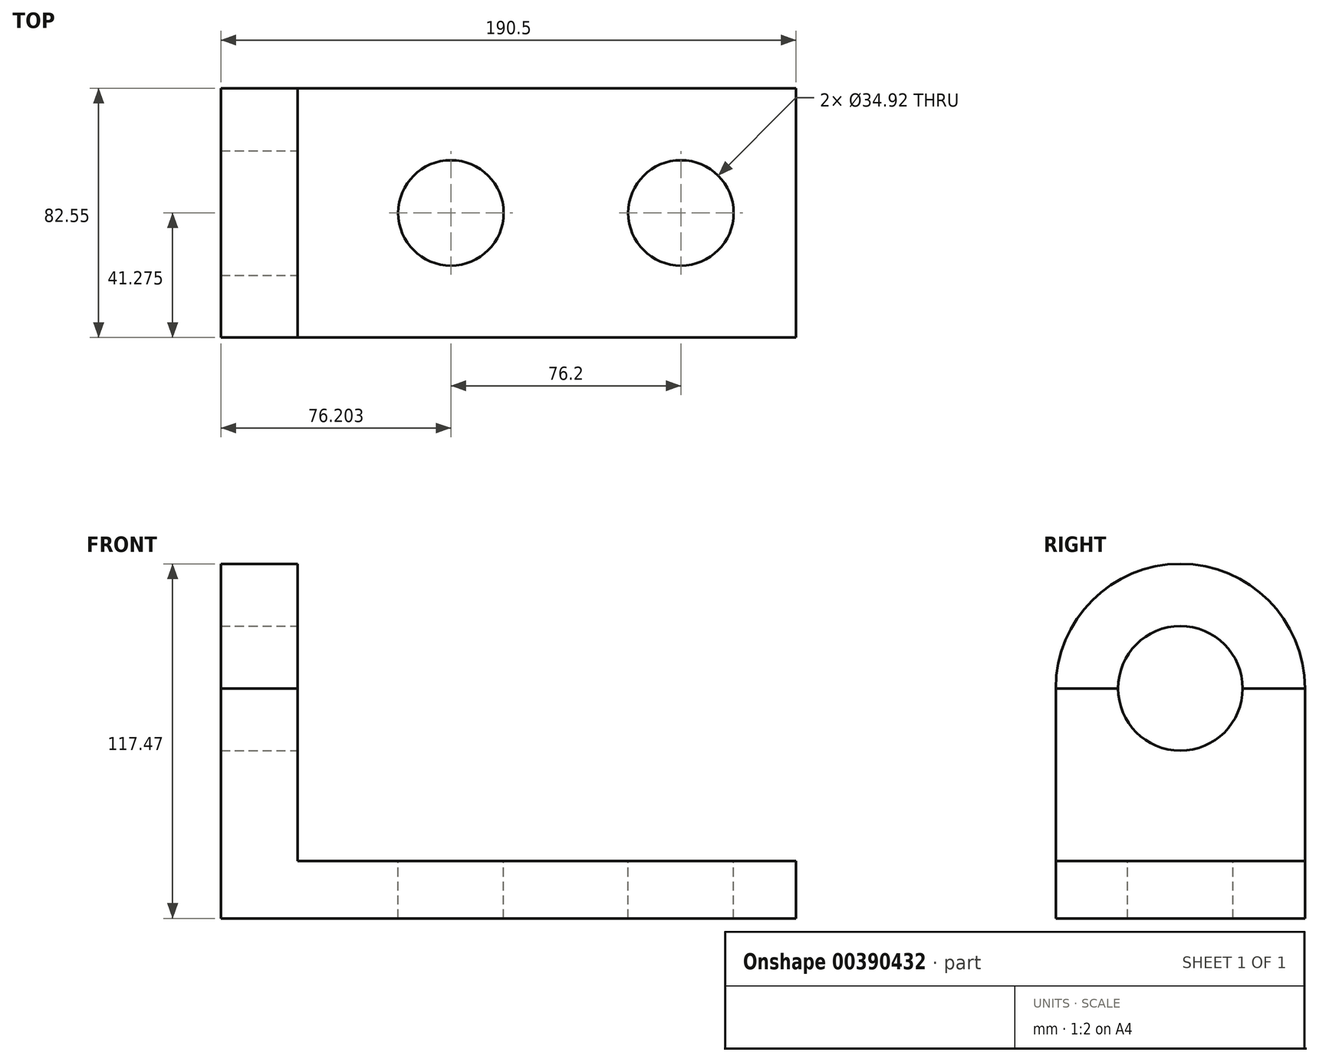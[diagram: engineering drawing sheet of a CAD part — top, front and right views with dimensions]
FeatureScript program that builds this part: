
annotation { "Feature Type Name" : "Feature", "Feature Type Description" : "" }
export const myFeature = defineFeature(function(context is Context, id is Id, definition is map)
    precondition{}
    {
        {
            var Q0;
            Q0=qCreatedBy(makeId("Top.planeOp"),FACE);
            var sketch = newSketch(context, id + "F0", { "sketchPlane" : qUnion([Q0])});
            skLineSegment(sketch, "E0", {"start": v(-43.38, 45.06) * mm, "end": v(-43.38, -37.5) * mm});
            skLineSegment(sketch, "E1", {"start": v(-43.38, -37.5) * mm, "end": v(147.12, -37.5) * mm});
            skLineSegment(sketch, "E2", {"start": v(147.12, -37.5) * mm, "end": v(147.12, 45.06) * mm});
            skLineSegment(sketch, "E3", {"start": v(147.12, 45.06) * mm, "end": v(-43.38, 45.06) * mm});
            skSolve(sketch);
        }
        {
            var Q0;
            Q0=makeQuery(id+"F0.imprint","IMPRINT",FACE,{"disambiguationData":[TD([[makeQuery(id+"F0.imprint","IMPRINT",EDGE,{"derivedFrom":sQuery(id+"F0.wireOp",EDGE,"E0")}),1.0]])]});
            extrude(context, id + "F1", {"entities" : qUnion([Q0]), "depth" : 19.05 * mm});
        }
        {
            var Q0;
            Q0=makeQuery(id+"F1.opExtrude","CAP_FACE",FACE,{"disambiguationData":[OSD([sQuery(id+"F0.wireOp",EDGE,"E0"),sQuery(id+"F0.wireOp",EDGE,"E1"),sQuery(id+"F0.wireOp",EDGE,"E2"),sQuery(id+"F0.wireOp",EDGE,"E3")])],"isStart":false});
            var sketch = newSketch(context, id + "F2", { "sketchPlane" : qUnion([Q0])});
            skLineSegment(sketch, "E4", {"start": v(-43.38, 45.06) * mm, "end": v(-17.98, 45.06) * mm});
            skLineSegment(sketch, "E5", {"start": v(-17.98, 45.06) * mm, "end": v(-17.98, -37.5) * mm});
            skLineSegment(sketch, "E6", {"start": v(-17.98, -37.5) * mm, "end": v(-43.38, -37.5) * mm});
            skLineSegment(sketch, "E7", {"start": v(-43.38, -37.5) * mm, "end": v(-43.38, 45.06) * mm});
            skSolve(sketch);
        }
        {
            var Q0;
            Q0=makeQuery(id+"F2.imprint","IMPRINT",FACE,{"disambiguationData":[TD([[makeQuery(id+"F2.imprint","IMPRINT",EDGE,{"derivedFrom":sQuery(id+"F2.wireOp",EDGE,"E4")}),1.0]])]});
            extrude(context, id + "F3", {"entities" : qUnion([Q0]), "operationType" : NewBodyOperationType.ADD, "depth" : 57.15 * mm});
        }
        {
            var Q0;
            Q0=makeQuery(id+"F3.opExtrude","SWEPT_FACE",FACE,{"disambiguationData":[OSD([sQuery(id+"F2.wireOp",EDGE,"E5")])]});
            var sketch = newSketch(context, id + "F4", { "sketchPlane" : qUnion([Q0])});
            skCircle(sketch, "E8", {"center": v(3.78, 76.2) * mm, "radius": 41.28 * mm});
            skSolve(sketch);
        }
        {
            var Q0;
            {var subQ1=sQuery(id+"F2.wireOp",EDGE,"E5");var subQ2=makeQuery(id+"F3.opExtrude","CAP_EDGE",EDGE,{"disambiguationData":[OSD([subQ1])],"isStart":false});Q0=makeQuery(id+"F4.imprint","IMPRINT",FACE,{"disambiguationData":[TD([[makeQuery(id+"F4.imprint","IMPRINT",EDGE,{"derivedFrom":subQ2}),-1.0]])]});}
            extrude(context, id + "F5", {"entities" : qUnion([Q0]), "oppositeDirection" : true, "depth" : 25.4 * mm});
        }
        {
            var Q0;
            Q0=makeQuery(id+"F5.opExtrude","CAP_FACE",FACE,{"disambiguationData":[OSD([sQuery(id+"F2.wireOp",EDGE,"E5"),sQuery(id+"F4.wireOp",EDGE,"E8")])],"isStart":true});
            var sketch = newSketch(context, id + "F6", { "sketchPlane" : qUnion([Q0])});
            skCircle(sketch, "E9", {"center": v(3.78, 76.2) * mm, "radius": 20.64 * mm});
            skSolve(sketch);
        }
        {
            var Q0;
            {var subQ0=sQuery(id+"F6.wireOp",EDGE,"E9");var subQ1=makeQuery(id+"F5.opExtrude","CAP_EDGE",EDGE,{"disambiguationData":[OSD([sQuery(id+"F2.wireOp",EDGE,"E5")])],"isStart":true});var subQ2=makeQuery(id+"F6.imprint","INTERSECT",VERTEX,{"disambiguationData":[OD(0.0)],"derivedFrom":[subQ1,subQ0]});Q0=makeQuery(id+"F6.imprint","IMPRINT",FACE,{"disambiguationData":[TD([[makeQuery(id+"F6.imprint","IMPRINT",EDGE,{"disambiguationData":[TD([[subQ2,-1.0]])],"derivedFrom":subQ0}),1.0]])]});}
            extrude(context, id + "F7", {"entities" : qUnion([Q0]), "operationType" : NewBodyOperationType.REMOVE, "oppositeDirection" : true, "depth" : 25.4 * mm});
        }
        {
            var Q0;
            Q0=makeQuery(id+"F3.opExtrude","SWEPT_FACE",FACE,{"disambiguationData":[OSD([sQuery(id+"F2.wireOp",EDGE,"E5")])]});
            var sketch = newSketch(context, id + "F8", { "sketchPlane" : qUnion([Q0])});
            skCircle(sketch, "E10", {"center": v(3.78, 76.2) * mm, "radius": 20.64 * mm});
            skSolve(sketch);
        }
        {
            var Q0;
            {var subQ0=sQuery(id+"F8.wireOp",EDGE,"E10");var subQ1=makeQuery(id+"F3.opExtrude","CAP_EDGE",EDGE,{"disambiguationData":[OSD([sQuery(id+"F2.wireOp",EDGE,"E5")])],"isStart":false});var subQ2=makeQuery(id+"F8.imprint","INTERSECT",VERTEX,{"disambiguationData":[OD(0.0)],"derivedFrom":[subQ1,subQ0]});Q0=makeQuery(id+"F8.imprint","IMPRINT",FACE,{"disambiguationData":[TD([[makeQuery(id+"F8.imprint","IMPRINT",EDGE,{"disambiguationData":[TD([[subQ2,1.0]])],"derivedFrom":subQ0}),1.0]])]});}
            extrude(context, id + "F9", {"entities" : qUnion([Q0]), "operationType" : NewBodyOperationType.REMOVE, "oppositeDirection" : true, "depth" : 25.4 * mm});
        }
        {
            var Q0;
            Q0=makeQuery(id+"F1.opExtrude","CAP_FACE",FACE,{"disambiguationData":[OSD([sQuery(id+"F0.wireOp",EDGE,"E0"),sQuery(id+"F0.wireOp",EDGE,"E1"),sQuery(id+"F0.wireOp",EDGE,"E2"),sQuery(id+"F0.wireOp",EDGE,"E3")])],"isStart":false});
            var sketch = newSketch(context, id + "F10", { "sketchPlane" : qUnion([Q0])});
            skCircle(sketch, "E11", {"center": v(109.02, 3.78) * mm, "radius": 17.46 * mm});
            skSolve(sketch);
        }
        {
            var Q0;
            Q0=makeQuery(id+"F10.imprint","IMPRINT",FACE,{"disambiguationData":[TD([[makeQuery(id+"F10.imprint","IMPRINT",EDGE,{"derivedFrom":sQuery(id+"F10.wireOp",EDGE,"E11")}),1.0]])]});
            extrude(context, id + "F11", {"entities" : qUnion([Q0]), "operationType" : NewBodyOperationType.REMOVE, "oppositeDirection" : true, "depth" : 25.4 * mm});
        }
        {
            var Q0;
            Q0=makeQuery(id+"F1.opExtrude","CAP_FACE",FACE,{"disambiguationData":[OSD([sQuery(id+"F0.wireOp",EDGE,"E0"),sQuery(id+"F0.wireOp",EDGE,"E1"),sQuery(id+"F0.wireOp",EDGE,"E2"),sQuery(id+"F0.wireOp",EDGE,"E3")])],"isStart":false});
            var sketch = newSketch(context, id + "F12", { "sketchPlane" : qUnion([Q0])});
            skCircle(sketch, "E12", {"center": v(32.82, 3.78) * mm, "radius": 17.46 * mm});
            skSolve(sketch);
        }
        {
            var Q0;
            Q0=makeQuery(id+"F12.imprint","IMPRINT",FACE,{"disambiguationData":[TD([[makeQuery(id+"F12.imprint","IMPRINT",EDGE,{"derivedFrom":sQuery(id+"F12.wireOp",EDGE,"E12")}),1.0]])]});
            extrude(context, id + "F13", {"entities" : qUnion([Q0]), "operationType" : NewBodyOperationType.REMOVE, "oppositeDirection" : true, "depth" : 25.4 * mm});
        }
    });
